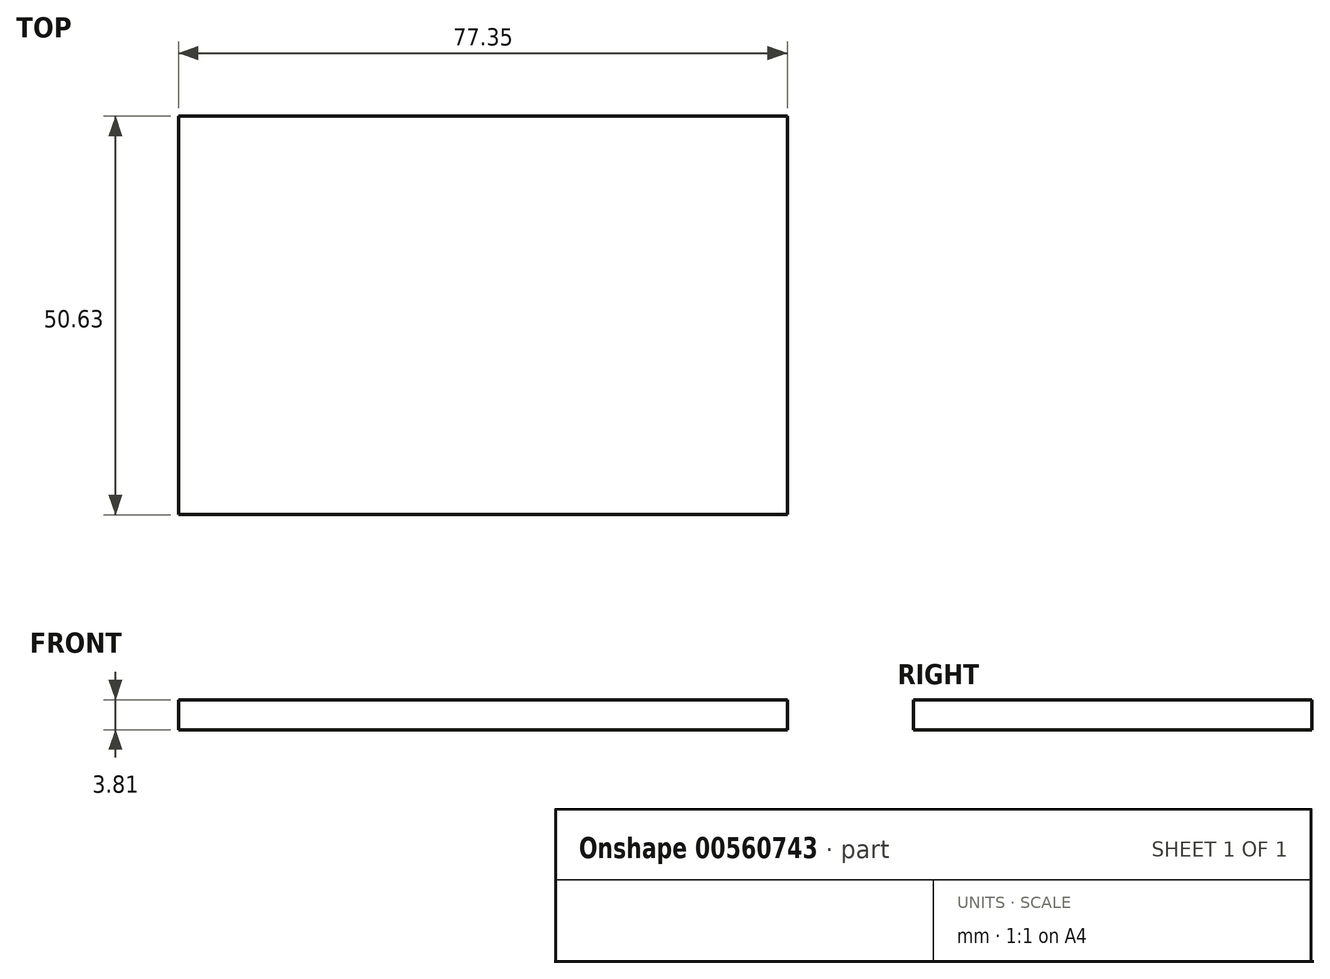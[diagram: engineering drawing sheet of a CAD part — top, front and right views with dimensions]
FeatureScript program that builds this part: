
annotation { "Feature Type Name" : "Feature", "Feature Type Description" : "" }
export const myFeature = defineFeature(function(context is Context, id is Id, definition is map)
    precondition{}
    {
        {
            var Q0;
            Q0=qCreatedBy(makeId("Top.planeOp"),FACE);
            var sketch = newSketch(context, id + "F0", { "sketchPlane" : qUnion([Q0])});
            skLineSegment(sketch, "E0", {"start": v(-45.31, -34.32) * mm, "end": v(30.9, -34.32) * mm});
            skLineSegment(sketch, "E1", {"start": v(30.9, -34.32) * mm, "end": v(30.9, 16.3) * mm});
            skLineSegment(sketch, "E2", {"start": v(30.9, 16.3) * mm, "end": v(-46.45, 16.3) * mm});
            skLineSegment(sketch, "E3", {"start": v(-46.45, 16.3) * mm, "end": v(-46.45, -34.32) * mm});
            skLineSegment(sketch, "E4", {"start": v(-46.45, -34.32) * mm, "end": v(-45.31, -34.32) * mm});
            skSolve(sketch);
        }
        {
            var Q0;
            Q0=makeQuery(id+"F0.imprint","IMPRINT",FACE,{"disambiguationData":[TD([[makeQuery(id+"F0.imprint","IMPRINT",EDGE,{"derivedFrom":sQuery(id+"F0.wireOp",EDGE,"E0")}),1.0]])]});
            extrude(context, id + "F1", {"entities" : qUnion([Q0]), "depth" : 3.8 * mm, "offsetDistance" : 25.4 * mm});
        }
    });
